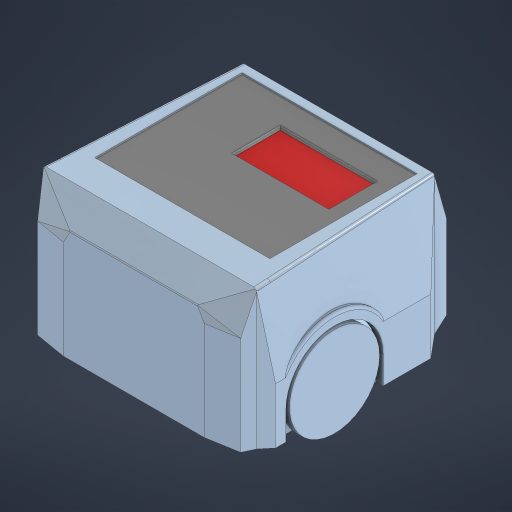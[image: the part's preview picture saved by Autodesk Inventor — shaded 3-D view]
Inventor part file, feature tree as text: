
AUTODESK INVENTOR PART (.ipt)
format: ipt  version: 2024 (Build 280153000, 153)  size: 2,024,448 bytes
history: native  units: mm
features: other x56, sketch x42, extrude x40, loft x18, fillet x8, plane x1
ambient origin geometry x8: Origin, YZ Plane, XZ Plane, XY Plane, X Axis, Y Axis, Z Axis, Center Point
bodies: Body1 (feature_tree), Body2 (feature_tree)
feature tree (165):
  other  "Sólido1"
  extrude  "Base"  Depth=10.0mm TaperAngle=0.0deg
  extrude  "Llantas"  Depth=70.0mm
  extrude  "Carroceria"  Depth=75.0mm
  extrude  "Extrusión30"  Depth=150.0mm
  extrude  "Extrusión31"  Depth=10.0mm TaperAngle=0.0deg
  extrude  "Extrusión32"  Depth=8.726646mm
  extrude  "Extrusión33"  Depth=40.0mm
  extrude  "Extrusión34"  Depth=15.0mm
  extrude  "Extrusión35"  Depth=50.0mm
  extrude  "Extrusión38"  Depth=11.34464mm
  extrude  "Extrusión39"  Depth=5.0mm
  extrude  "Extrusión100"  Depth=3.0mm
  extrude  "Extrusión102"  Depth=5.0mm
  extrude  "Extrusión103"  Depth=3.0mm
  extrude  "Extrusión104"  TaperAngle=0.0deg  [1 undecoded]
  loft  "Solevación32"
  loft  "Solevación33"
  extrude  "Extrusión43"  TaperAngle=0.0deg  [1 undecoded]
  extrude  "Extrusión96"  Depth=3.0mm
  extrude  "Extrusión110"  Depth=3.0mm
  extrude  "Extrusión90"  Depth=3.0mm
  extrude  "Extrusión94"  Depth=3.0mm
  extrude  "Extrusión95"  Depth=3.0mm
  loft  "Solevación10"
  loft  "Solevación11"
  extrude  "Extrusión53"  TaperAngle=0.0deg  [1 undecoded]
  extrude  "Extrusión93"  TaperAngle=0.0deg  [1 undecoded]
  loft  "Solevación8"
  loft  "Solevación9"
  extrude  "Extrusión84"  Depth=80.0mm TaperAngle=0.0deg
  extrude  "Extrusión64"  Depth=5.0mm
  extrude  "Extrusión65"  Depth=5.0mm TaperAngle=0.0deg
  extrude  "Extrusión67"  Depth=5.0mm TaperAngle=0.0deg
  extrude  "Extrusión111"  Depth=6.0mm
  plane  "Plano de trabajo5"
  extrude  "Extrusión98"  Depth=3.0mm
  loft  "Solevación18"
  loft  "Solevación19"
  loft  "Solevación20"
  loft  "Solevación21"
  loft  "Solevación22"
  loft  "Solevación23"
  loft  "Solevación24"
  loft  "Solevación30"
  loft  "Solevación26"
  loft  "Solevación31"
  loft  "Solevación34"
  loft  "Solevación35"
  fillet  "Empalme1"  Radius=100.0mm
  fillet  "Empalme2"  [1 undecoded]
  fillet  "Empalme3"  Radius=30.0mm
  fillet  "Empalme4"  Radius=10.0mm
  fillet  "Empalme5"  Radius=11.34464mm
  fillet  "Empalme6"  Radius=10.0mm
  fillet  "Empalme7"  Radius=11.34464mm
  extrude  "Extrusión105"  TaperAngle=0.0deg  [1 undecoded]
  extrude  "Extrusión106"  Depth=10.0mm TaperAngle=0.0deg
  extrude  "Extrusión107"  Depth=12.0mm
  extrude  "Extrusión108"  Depth=10.0mm
  extrude  "Extrusión109"  Depth=12.0mm TaperAngle=0.0deg
  extrude  "Extrusión112"  TaperAngle=0.0deg  [1 undecoded]
  extrude  "Extrusión113"  Depth=12.0mm
  extrude  "Extrusión114"  Depth=12.0mm
  extrude  "Extrusión115"  Depth=12.0mm
  extrude  "Extrusión116"  Depth=12.0mm
  extrude  "Extrusión117"  Depth=12.0mm TaperAngle=0.0deg
  fillet  "Empalme8"  Radius=5.0mm
  sketch  "Boceto Base"  dims[d424=37.5mm d425=5.0mm]
  sketch  "Boceto Llantas"  dims[d426=5.0mm d427=5.0mm]
  sketch  "Boceto Carroceria"  dims[d428=5.0mm d429=15.0mm d430=0.0mm d431=10.0mm d432=5.0mm d433=85.592mm d434=0.0mm d439=10.0mm d440=0.0mm d494=10.0mm d495=0.0mm d514=100.0mm d515=0.0mm d530=30.0deg d531=30.0mm d532=10.0mm d533=0.0mm d534=0.0mm d535=90.0deg d536=0.0mm d537=90.0deg d538=0.0mm d539=90.0deg d540=0.0mm d541=90.0deg d542=11.34464mm d543=10.0mm d544=0.0mm d545=11.34464mm d546=0.0mm d547=10.0mm d548=0.0mm d549=5.0mm d550=10.0mm d551=105.0mm d552=0.0mm d553=0.0mm d554=90.0deg d559=0.0mm d560=90.0deg d595=20.0mm d596=20.0mm d597=30.0mm d598=30.0mm d599=5.0mm d600=0.0mm d611=5.0mm d612=0.0mm d613=90.0deg d614=0.0mm d615=90.0deg d616=0.0mm d617=90.0deg d618=0.0mm d619=90.0deg d620=0.0mm d621=90.0deg d622=0.0mm d623=90.0deg d624=0.0mm d625=90.0deg d626=0.0mm d627=90.0deg d628=0.0mm d629=90.0deg d630=0.0mm d631=90.0deg d632=5.0mm d633=0.0mm d634=90.0deg d635=0.0mm d636=90.0deg d637=0.0mm d638=90.0deg d639=0.0mm d640=90.0deg d645=0.0mm d646=90.0deg d647=0.0mm d648=90.0deg d653=20.0mm d654=85.0mm d655=42.5mm d656=70.0mm d657=200.0mm d658=0.0mm d669=40.0mm d670=0.0mm d671=0.0mm d672=90.0deg d673=0.0mm d674=90.0deg d676=0.0mm d677=90.0deg d680=0.0mm d681=90.0deg d684=5.0mm d685=0.0mm d686=5.0mm d687=0.0mm d688=0.0mm d689=90.0deg d690=0.0mm d691=90.0deg d692=0.0mm d693=90.0deg d694=0.0mm d695=90.0deg d697=0.0mm d698=90.0deg d699=0.0mm d700=90.0deg d701=0.0mm d702=90.0deg d703=0.0mm d704=90.0deg d705=2.0mm d706=2.0mm d707=2.0mm d708=2.0mm d709=2.0mm d710=2.0mm d711=2.0mm d712=100.0mm d713=0.0mm d714=100.0mm d715=0.0mm d716=10.0mm d717=15.0mm d718=10.0mm d719=10.0mm d720=15.0mm d723=10.0mm d724=10.0mm d725=3.0mm d726=5.0mm d727=5.0mm d728=3.0mm d729=5.0mm d730=5.0mm d731=5.0mm d732=0.0mm d733=5.0mm d734=10.0mm d735=0.0mm d737=5.0mm d738=10.0mm d739=0.0mm d740=3.0mm d741=120.0deg d742=120.0deg d743=3.0mm d744=120.0deg d745=3.0mm d746=120.0deg d747=2.598mm d748=5.196152mm d749=3.0mm d750=2.0mm d751=0.0mm d752=3.0mm d753=3.0mm d754=120.0deg d755=3.0mm d756=120.0deg d757=3.0mm d758=3.0mm d759=120.0deg d760=3.0mm d761=2.598mm d762=2.0mm d763=0.0mm d764=0.0mm d765=90.0deg d766=0.0mm d767=90.0deg d768=10.0mm d769=0.0mm d770=1.0mm d771=0.0mm d772=10.5mm d774=35.0mm d778=3.0mm d779=0.0mm d783=65.0mm d784=0.0mm d785=5.0mm d786=0.0mm d787=0.0mm d788=35.0mm d789=65.0mm d790=5.0mm d791=0.0mm d792=30.0mm d793=12.5mm d794=0.0mm d795=12.0mm d796=18.0mm d797=70.0mm d64=0.5mm d65=0.872665mm d66=0.5mm d67=0.872665mm d229=0.5mm d230=0.872665mm d231=0.5mm d232=0.872665mm d284=0.5mm d285=0.872665mm d286=0.5mm d287=0.872665mm d288=0.5mm d289=0.872665mm d290=0.5mm d342=0.5mm d343=0.872665mm d344=0.5mm d345=0.872665mm d352=0.5mm d353=0.872665mm d354=0.5mm d355=0.872665mm d364=0.5mm d365=0.872665mm d366=0.5mm d367=0.872665mm d386=0.5mm d387=0.872665mm d388=0.5mm d389=0.872665mm d472=0.5mm d473=0.872665mm d474=0.5mm d475=0.872665mm d525=0.5mm d526=0.872665mm d527=0.5mm d528=0.872665mm]
  sketch  "Boceto28"  dims[d0=160.0mm d2=10.0mm d3=0.0mm]
  sketch  "Boceto30"  dims[d4=70.0mm d5=70.0mm]
  sketch  "Boceto31"  dims[d6=20.0mm d7=75.0mm]
  sketch  "Boceto32"  dims[d8=80.0mm d9=150.0mm]
  sketch  "Boceto33"  dims[d10=25.0mm d11=10.0mm d12=0.0mm]
  sketch  "Boceto34"  dims[d13=30.0mm d14=8.726646mm]
  sketch  "Boceto37"  dims[d15=11.34464mm d16=40.0mm]
  sketch  "Boceto38"  dims[d17=15.0mm d18=15.0mm]
  sketch  "Boceto43"  dims[d19=6.0mm d20=50.0mm]
  sketch  "Boceto54"  dims[d21=8.726646mm d22=11.34464mm]
  sketch  "Boceto64"  dims[d23=6.0mm d24=5.0mm]
  sketch  "Boceto65"  dims[d25=10.0mm d26=0.0mm d291=3.0mm]
  sketch  "Boceto67"  dims[d292=5.0mm d293=5.0mm]
  sketch  "Boceto106"  dims[d294=3.0mm d295=5.0mm]
  sketch  "Boceto114"  dims[d297=3.0mm d298=0.0mm]
  sketch  "Boceto117"  dims[d299=0.0mm d300=0.0mm]
  sketch  "Boceto118"  dims[d301=0.0mm d303=5.0mm]
  sketch  "Boceto119"  dims[d304=3.0mm d305=0.0mm]
  sketch  "Boceto120"  dims[d306=5.0mm d307=3.0mm]
  sketch  "Boceto125"  dims[d308=5.0mm d309=3.0mm]
  sketch  "Boceto129"  dims[d310=5.0mm d311=3.0mm]
  other  "Aristas31"
  other  "Aristas32"
  other  "Aristas33"
  other  "Aristas34"
  other  "Aristas35"
  other  "Aristas36"
  other  "Aristas37"
  other  "Aristas38"
  other  "Aristas39"
  sketch  "Boceto131"  dims[d312=5.0mm d313=3.0mm]
  other  "Aristas40"
  other  "Aristas47"
  other  "Aristas48"
  other  "Sólido8"
  other  "Aristas49"
  other  "Aristas50"
  sketch  "Boceto132"  dims[d314=3.0mm d315=5.0mm]
  sketch  "Boceto135"  dims[d316=0.0mm d317=0.0mm]
  other  "Aristas57"
  other  "Aristas58"
  other  "Aristas59"
  other  "Aristas60"
  sketch  "Boceto138"  dims[d318=0.0mm d319=0.0mm]
  sketch  "Boceto139"  dims[d320=0.0mm d321=0.0mm]
  other  "Aristas65"
  other  "Aristas66"
  other  "Aristas67"
  other  "Aristas68"
  other  "Aristas69"
  other  "Aristas70"
  other  "Aristas71"
  other  "Aristas72"
  sketch  "Boceto142"  dims[d322=0.0mm d323=0.0mm]
  sketch  "Boceto143"  dims[d324=0.0mm d325=0.0mm]
  sketch  "Boceto144"  dims[d326=0.0mm d327=0.1mm d328=0.0mm]
  sketch  "Boceto145"  dims[d329=0.0mm d330=80.0mm d331=0.0mm]
  sketch  "Boceto146"  dims[d332=71.0mm d333=0.0mm d334=5.0mm]
  sketch  "Boceto148"  dims[d335=5.0mm d336=5.0mm d337=0.0mm]
  other  "Aristas73"
  other  "Aristas74"
  other  "Aristas75"
  other  "Aristas76"
  sketch  "Boceto149"  dims[d338=100.0mm d339=0.0mm d340=5.0mm d341=0.0mm]
  other  "Aristas77"
  other  "Aristas78"
  other  "Aristas79"
  other  "Aristas80"
  sketch  "Boceto150"  dims[d346=5.0mm d347=0.0mm d348=6.0mm]
  sketch  "Boceto152"  dims[d349=70.0mm d350=0.0mm d368=3.0mm]
  sketch  "Boceto153"  dims[d369=5.0mm d370=47.5mm]
  sketch  "Boceto154"  dims[d371=5.0mm d372=5.0mm]
  sketch  "Boceto155"  dims[d373=5.0mm d374=15.0mm d375=0.0mm]
  sketch  "Boceto156"  dims[d396=70.0mm d397=0.0mm d422=3.0mm]
  other  "Finish1"
  other  "Finish2"
  other  "Finish3"
  other  "Finish4"
  other  "Finish5"
  other  "Finish6"
  other  "Finish7"
  other  "Finish8"
  other  "Finish9"
  other  "Finish10"
  other  "Finish11"
  other  "Finish12"
  other  "Finish13"
  other  "Finish14"
  other  "Finish15"
  other  "Finish16"
  other  "Finish17"
  other  "Finish18"
  other  "Finish19"
  other  "Finish20"
note: 7 required parameter values undecoded (feature->parameter linkage not recoverable at this tier; creation-order binding heuristic only, values carry confidence <= 0.55)
